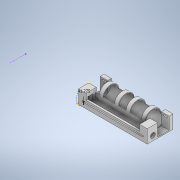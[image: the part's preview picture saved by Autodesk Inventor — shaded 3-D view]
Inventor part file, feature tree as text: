
AUTODESK INVENTOR PART (.ipt)
format: ipt  version: 2020 (Build 240168000, 168)  size: 638,976 bytes
history: native  units: mm
features: sketch x31, extrude x20, fillet x1, plane x1
ambient origin geometry x8: Origin, YZ Plane, XZ Plane, XY Plane, X Axis, Y Axis, Z Axis, Center Point
bodies: Solid1 (feature_tree)
feature tree (53):
  extrude  "Extrusion1"  Depth=27.0mm
  extrude  "Extrusion2"  Depth=25.0mm
  sketch  "Sketch3"  dims[d4=10.0mm d5=0.0mm d6=10.0mm]
  sketch  "Sketch4"  dims[d7=10.0mm d8=0.0mm d9=5.0mm]
  sketch  "Sketch5"  dims[d10=11.0mm d11=5.0mm]
  extrude  "Extrusion3"  Depth=10.0mm
  extrude  "Extrusion4"  Depth=5.0mm
  extrude  "Extrusion5"  Depth=5.0mm
  extrude  "Extrusion6"  Depth=10.0mm
  fillet  "Fillet1"  Radius=7.5mm
  extrude  "Extrusion7"  Depth=10.0mm TaperAngle=0.0deg
  sketch  "Sketch11"  dims[d28=3.0mm d29=12.0mm]
  extrude  "Extrusion8"  Depth=2.0mm
  sketch  "Sketch13"  dims[d33=41.275mm d34=7.0mm]
  extrude  "Extrusion9"  Depth=3.0mm
  extrude  "Extrusion10"  Depth=12.0mm
  sketch  "Sketch16"  dims[d41=67.0mm d42=0.0mm d43=38.0mm]
  sketch  "Sketch17"  dims[d44=38.0mm d45=38.0mm]
  extrude  "Extrusion11"  Depth=12.0mm
  sketch  "Sketch19"  dims[d49=10.0mm d50=32.0mm d51=0.0mm]
  extrude  "Extrusion12"  Depth=23.5mm TaperAngle=0.0deg
  extrude  "Extrusion13"  Depth=7.0mm
  sketch  "Sketch22"  dims[d57=41.5mm]
  extrude  "Extrusion14"  Depth=4.5mm
  extrude  "Extrusion15"  Depth=3.0mm
  extrude  "Extrusion16"  Depth=67.0mm
  extrude  "Extrusion17"  Depth=38.0mm
  extrude  "Extrusion18"  Depth=10.0mm
  sketch  "Sketch28"  dims[d66=41.5mm]
  sketch  "Sketch29"  dims[d67=140.0mm d68=0.0mm]
  extrude  "Extrusion19"  Depth=32.0mm TaperAngle=0.0deg
  plane  "Work Plane1"
  extrude  "Extrusion20"  Depth=30.0mm TaperAngle=0.0deg
  sketch  "Sketch1"  dims[d0=35.0mm d1=27.0mm]
  sketch  "Sketch2"  dims[d2=25.0mm d3=12.7mm]
  sketch  "Sketch6"  dims[d12=150.0mm d13=0.0mm d14=10.0mm d15=7.5mm d16=0.0mm]
  sketch  "Sketch7"  dims[d17=10.0mm d18=0.0mm d19=10.0mm d20=0.0mm]
  sketch  "Sketch8"  dims[d21=2.0mm d22=7.0mm]
  sketch  "Sketch9"  dims[d23=14.0mm d24=3.0mm]
  sketch  "Sketch10"  dims[d25=140.0mm d26=0.0mm d27=12.0mm]
  sketch  "Sketch12"  dims[d30=3.0mm d31=23.5mm d32=0.0mm]
  sketch  "Sketch14"  dims[d35=4.5mm d36=0.0mm d37=7.0mm]
  sketch  "Sketch15"  dims[d38=4.5mm d39=0.0mm d40=3.0mm]
  sketch  "Sketch18"  dims[d46=30.0mm d47=0.0mm d48=10.0mm]
  sketch  "Sketch20"  dims[d52=10.0mm d53=0.0mm d54=30.0mm d55=0.0mm]
  sketch  "Sketch21"  dims[d56=38.0mm]
  sketch  "Sketch23"  dims[d58=38.0mm]
  sketch  "Sketch24"  dims[d59=38.0mm]
  sketch  "Sketch25"  dims[d60=45.0mm d61=0.0mm]
  sketch  "Sketch26"  dims[d62=5.0mm d63=0.0mm]
  sketch  "Sketch27"  dims[d64=45.0mm d65=0.0mm]
  sketch  "Sketch30"  dims[d69=10.0mm]
  sketch  "Sketch31"  dims[d70=10.0mm d71=10.0mm d72=10.0mm d73=10.0mm d74=10.0mm d75=10.0mm d76=10.0mm d77=10.0mm d78=10.0mm d79=10.0mm d80=10.0mm d81=10.0mm d82=19.0mm d83=0.0mm d84=0.5mm d85=0.872665mm]
